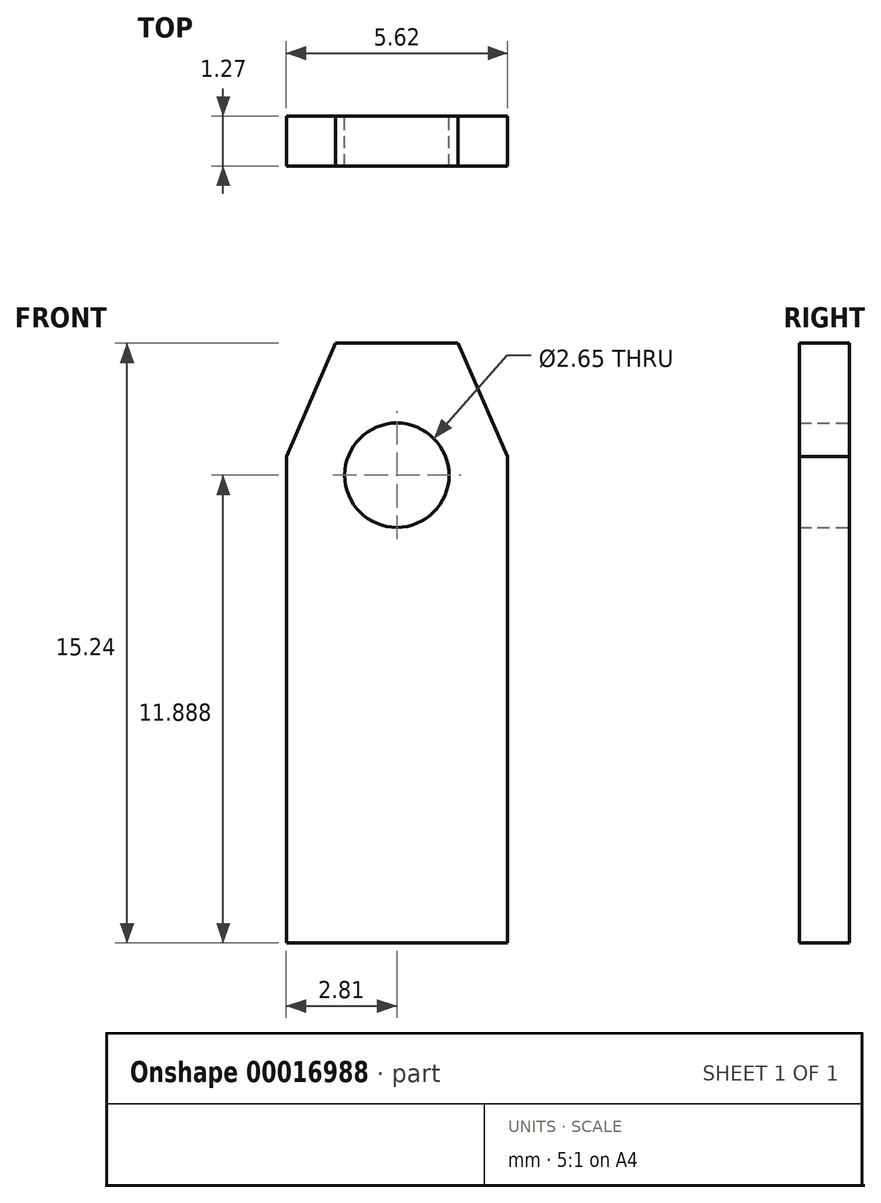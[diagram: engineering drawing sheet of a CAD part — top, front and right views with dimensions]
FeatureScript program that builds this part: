
annotation { "Feature Type Name" : "Feature", "Feature Type Description" : "" }
export const myFeature = defineFeature(function(context is Context, id is Id, definition is map)
    precondition{}
    {
        {
            var Q0;
            Q0=qCreatedBy(makeId("Front.planeOp"),FACE);
            var sketch = newSketch(context, id + "F0", { "sketchPlane" : qUnion([Q0])});
            skLineSegment(sketch, "E0", {"start": v(-2.8, 0) * mm, "end": v(-2.8, 12.36) * mm});
            skLineSegment(sketch, "E1", {"start": v(-2.8, 12.36) * mm, "end": v(-1.56, 15.24) * mm});
            skLineSegment(sketch, "E2", {"start": v(-1.56, 15.24) * mm, "end": v(0, 15.24) * mm});
            skLineSegment(sketch, "E3.MirrorCS", {"start": v(1.56, 15.24) * mm, "end": v(0, 15.24) * mm});
            skLineSegment(sketch, "E4.MirrorCS", {"start": v(2.8, 0) * mm, "end": v(2.8, 12.36) * mm});
            skLineSegment(sketch, "E5.MirrorCS", {"start": v(2.8, 12.36) * mm, "end": v(1.56, 15.24) * mm});
            skCircle(sketch, "E6", {"center": v(0, 11.89) * mm, "radius": 1.33 * mm});
            skLineSegment(sketch, "E7", {"start": v(-2.8, 0) * mm, "end": v(2.8, 0) * mm});
            skSolve(sketch);
        }
        {
            var Q0;
            Q0=makeQuery(id+"F0.imprint","IMPRINT",FACE,{"disambiguationData":[TD([[makeQuery(id+"F0.imprint","IMPRINT",EDGE,{"derivedFrom":sQuery(id+"F0.wireOp",EDGE,"E0")}),-1.0]])]});
            extrude(context, id + "F1", {"entities" : qUnion([Q0]), "depth" : 1.27 * mm});
        }
    });
